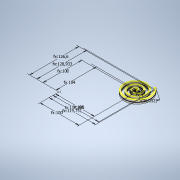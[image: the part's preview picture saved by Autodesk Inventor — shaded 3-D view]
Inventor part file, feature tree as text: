
AUTODESK INVENTOR PART (.ipt)
format: ipt  version: 2022.2 (Build 262287000, 287)  size: 495,104 bytes
history: native  units: mm
features: other x8, extrude x2, projected_geometry x2, sketch x1
ambient origin geometry x8: Origin, YZ Plane, XZ Plane, XY Plane, X Axis, Y Axis, Z Axis, Center Point
bodies: Body1 (feature_tree)
feature tree (13):
  other  "Rotor Wrap"
  other  "Rotor Profile"
  other  "Rotor Base"
  other  "Rotor Tip"
  extrude  "Rotor Wrap Extrusion"  Depth=213.1131mm
  other  "Rotor Wrap Draft"
  other  "Rotor Base Profile"
  extrude  "Tip Seal"  Depth=100.0mm
  other  "rotor_outer"
  other  "rotor_inner"
  projected_geometry  "Projected Loop1"
  sketch  "Sketch6"  dims[d0=0.0mm d1=213.1131mm d2=100.0mm d3=100.0mm d4=119.751226mm d5=128.93306mm d8=0.0mm d9=181.697174mm d10=117.865222mm d11=126.600039mm d14=4.873008mm d15=-4.873008mm d22=9.746017mm d23=0.0mm d24=104.0mm d25=-0.0mm d27=4.0mm d28=100.0mm d33=0.8mm d34=0.0mm d195=0.0mm d46=181.697174mm d50=0.0mm d51=213.1131mm d72=100.0mm d73=100.0mm d74=78.951679mm d78=98.0mm d79=100.0mm d82=73.06694mm d83=104.0mm d84=96.816901mm d87=1.5mm d98=5.844343mm d99=1.844343mm d100=9.746017mm d101=0.0mm d253=0.0mm d254=4.0mm d258=0.8mm d259=0.0mm d265=1.0mm d266=0.5mm d267=0.3mm d45=1.844343mm d47=5.844343mm d49=1.0mm]
  projected_geometry  "Projected Loop2"
